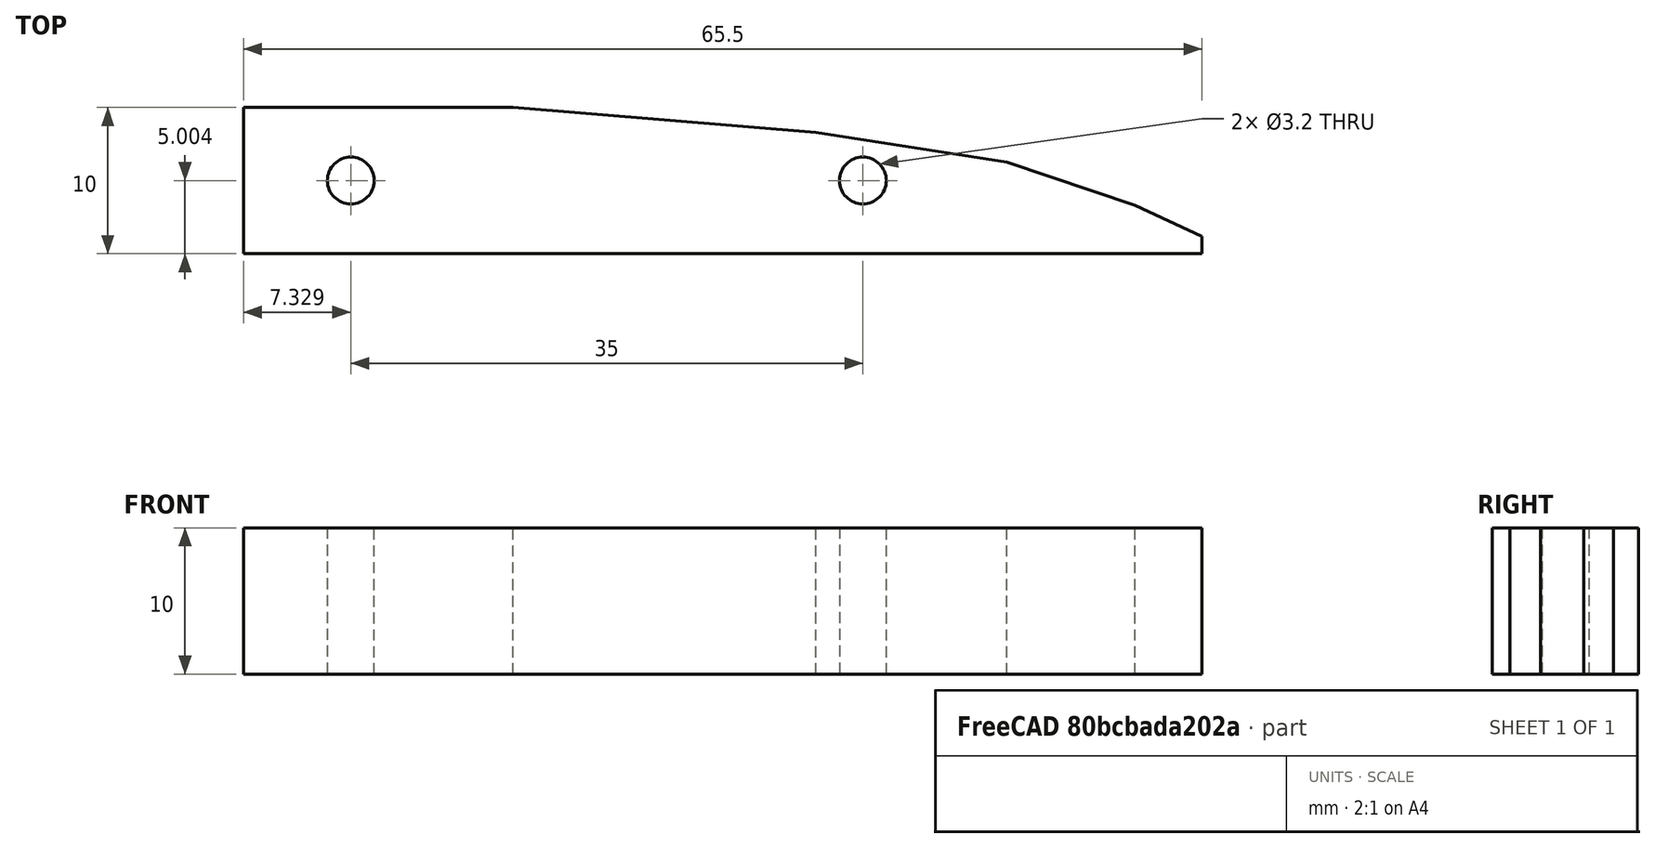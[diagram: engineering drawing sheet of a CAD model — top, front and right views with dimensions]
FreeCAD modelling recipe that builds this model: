
FCSTD DOCUMENT  (FreeCAD 0.17R13522 (Git))
Label: endstop
License: All rights reserved
LicenseURL: http://en.wikipedia.org/wiki/All_rights_reserved
objects: Sketcher::SketchObject×1, Part::Extrusion×1
note: 2 computed .brp shape members not serialized (recipe doc carries the construction recipe); baked Part::Feature solids carry a one-line shape summary decoded from their .brp

FEATURE [Sketcher::SketchObject] Sketch
  sketch-geometry (10):
    g0: LineSegment StartX=34.7716 StartY=28.7438 StartZ=0 EndX=34.7716 EndY=18.7438 EndZ=0
    g1: LineSegment StartX=34.7716 StartY=18.7438 StartZ=0 EndX=100.266 EndY=18.7438 EndZ=0
    g2: LineSegment StartX=100.266 StartY=18.7438 StartZ=0 EndX=100.266 EndY=19.9372 EndZ=0
    g3: LineSegment StartX=100.266 StartY=19.9372 StartZ=0 EndX=95.6895 EndY=22.0618 EndZ=0
    g4: LineSegment StartX=95.6895 StartY=22.0618 StartZ=0 EndX=86.9459 EndY=25.0036 EndZ=0
    g5: LineSegment StartX=86.9459 StartY=25.0036 StartZ=0 EndX=73.8715 EndY=27.0465 EndZ=0
    g6: LineSegment StartX=73.8715 StartY=27.0465 StartZ=0 EndX=53.1997 EndY=28.7438 EndZ=0
    g7: LineSegment StartX=53.1997 StartY=28.7438 StartZ=0 EndX=34.7716 EndY=28.7438 EndZ=0
    g8: Circle CenterX=42.0989 CenterY=23.7438 CenterZ=0 NormalX=0 NormalY=0 NormalZ=1 AngleXU=0 Radius=1.6
    g9: Circle CenterX=77.0989 CenterY=23.7438 CenterZ=0 NormalX=0 NormalY=0 NormalZ=1 AngleXU=0 Radius=1.6
  constraints (18):
    c: Vertical(g0)
    c: Coincident(g0,g1)
    c: Horizontal(g1)
    c: Coincident(g1,g2)
    c: Coincident(g2,g3)
    c: Coincident(g3,g4)
    c: Coincident(g4,g5)
    c: Coincident(g5,g6)
    c: Coincident(g6,g7)
    c: Coincident(g7,g0)
    c: Horizontal(g7)
    c: Distance(g0,g0) = 10
    c: Vertical(g2)
    c: Radius(g8) = 1.6
    c: Distance(g8,g1) = 5
    c: Equal(g8,g9)
    c: Distance(g9,g1) = 5
    c: Distance(g8,g9) = 35
FEATURE [Part::Extrusion] Extrude  label="endstop"
  Base = -> Sketch
  Dir = (0,0,1)
  DirMode = 2
  FaceMakerClass = Part::FaceMakerBullseye
  LengthFwd = 10
  LengthRev = 0
  Solid = true
  Symmetric = false
